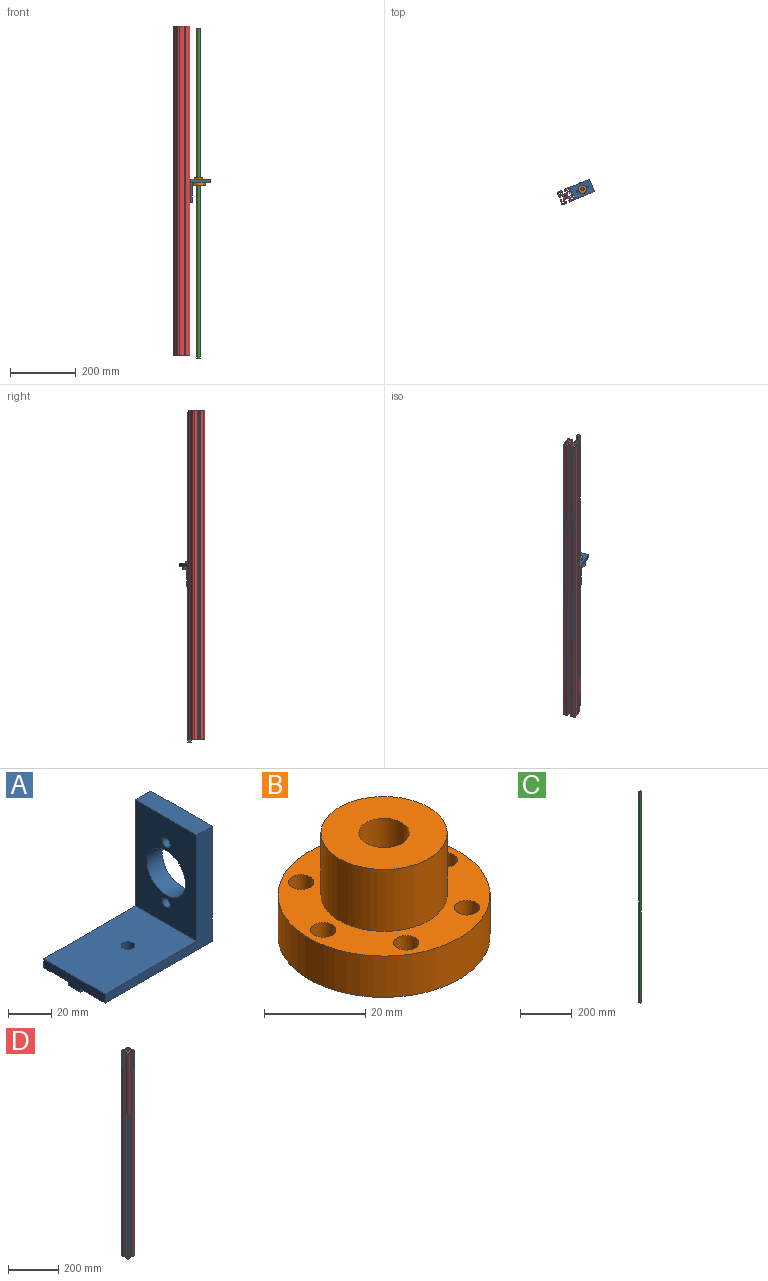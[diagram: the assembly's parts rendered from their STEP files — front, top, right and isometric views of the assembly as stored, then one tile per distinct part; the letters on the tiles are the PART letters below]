
ASSEMBLY  parts=4 mates=3
PART A: 16 faces, bbox 70x40x67 mm
  f0: plane 70x16.05mm, normal (0,0,-1), area 1123.5mm2, adj f1,f2,f3,f7
  f1: plane 40x7mm, normal (-1,0,0), area 215.8mm2, adj f0,f2,f4,f5,f6,f7,f8,f9
  f2: plane 70x65mm, normal (0,-1,0), area 950mm2, adj f0,f1,f3,f5,f11,f12
  f3: plane 67x40mm, normal (1,0,0), area 2079.7mm2, adj f0,f2,f4,f6,f7,f8,f9,f12
  f4: plane 70x65mm, normal (0,1,0), area 950mm2, adj f1,f3,f5,f6,f11,f12
  f5: plane 60x40mm, normal (0,0,1), area 2369.8mm2, adj f1,f2,f4,f10,f11
  f6: plane 70x16.05mm, normal (0,0,-1), area 1123.5mm2, adj f1,f3,f4,f8
  f7: plane 70x2mm, normal (0,-1,0), area 140mm2, adj f0,f1,f3,f9
  f8: plane 70x2mm, normal (0,1,0), area 140mm2, adj f1,f3,f6,f9
  f9: plane 70x7.9mm, normal (0,0,-1), area 522.8mm2, adj f1,f3,f7,f8,f10
  f10: cylinder r=3.1mm len=7mm, axis (0,0,-1), area 136.3mm2, adj f5,f9
  f11: plane 60x40mm, normal (-1,0,0), area 1863.9mm2, adj f2,f4,f5,f12,f13,f14,f15
  f12: plane 40x10mm, normal (0,0,1), area 400mm2, adj f2,f3,f4,f11
  f13: cylinder r=12.57mm len=25.15mm, axis (1,0,0), area 790.1mm2, adj f3,f11
  f14: cylinder r=2.5mm len=10mm, axis (-1,0,0), area 157.1mm2, adj f3,f11
  f15: cylinder r=2.5mm len=10mm, axis (-1,0,0), area 157.1mm2, adj f3,f11
PART B: 12 faces, bbox 42x42x25 mm
  f0: cylinder r=21mm len=42mm, axis (0,0,1), area 1319.5mm2, adj f1,f2
  f1: plane 42x42mm, normal (0,0,-1), area 1189.1mm2, adj f0,f5,f6,f7,f8,f9,f10,f11
  f2: plane 42x42mm, normal (0,0,1), area 776.8mm2, adj f0,f3,f6,f7,f8,f9,f10,f11
  f3: cylinder r=12.5mm len=25mm, axis (0,0,-1), area 1178.1mm2, adj f2,f4
  f4: plane 25x25mm, normal (0,0,1), area 412.3mm2, adj f3,f5
  f5: cylinder r=5mm len=25mm, axis (0,0,1), area 785.4mm2, adj f1,f4
  f6: cylinder r=2.5mm len=10mm, axis (0,0,-1), area 157.1mm2, adj f1,f2
  f7: cylinder r=2.5mm len=10mm, axis (0,0,-1), area 157.1mm2, adj f1,f2
  f8: cylinder r=2.5mm len=10mm, axis (0,0,-1), area 157.1mm2, adj f1,f2
  f9: cylinder r=2.5mm len=10mm, axis (0,0,-1), area 157.1mm2, adj f1,f2
  f10: cylinder r=2.5mm len=10mm, axis (0,0,-1), area 157.1mm2, adj f1,f2
  f11: cylinder r=2.5mm len=10mm, axis (0,0,-1), area 157.1mm2, adj f1,f2
PART C: 3 faces, bbox 10x10x1000 mm
  f0: cylinder r=5mm len=1000mm, axis (0,0,-1), area 31415.9mm2, adj f1,f2
  f1: plane 10x10mm, normal (0,0,1), area 78.5mm2, adj f0
  f2: plane 10x10mm, normal (0,0,-1), area 78.5mm2, adj f0
PART D: 87 faces, bbox 40x40x1000 mm
  f0: plane 1000x4mm, normal (0,-1,0), area 4000mm2, adj f1,f79,f85,f86
  f1: plane 1000x6mm, normal (-1,0,0), area 6000mm2, adj f0,f2,f85,f86
  f2: plane 1000x6mm, normal (0,1,0), area 6000mm2, adj f1,f3,f85,f86
  f3: plane 1000x4mm, normal (1,0,0), area 4000mm2, adj f2,f79,f85,f86
  f4: plane 1000x4mm, normal (0,1,0), area 4000mm2, adj f5,f80,f85,f86
  f5: plane 1000x6mm, normal (1,0,0), area 6000mm2, adj f4,f6,f85,f86
  f6: plane 1000x6mm, normal (0,-1,0), area 6000mm2, adj f5,f7,f85,f86
  f7: plane 1000x4mm, normal (-1,0,0), area 4000mm2, adj f6,f80,f85,f86
  f8: plane 1000x4mm, normal (1,0,0), area 4000mm2, adj f9,f81,f85,f86
  f9: plane 1000x6mm, normal (0,-1,0), area 6000mm2, adj f8,f10,f85,f86
  f10: plane 1000x6mm, normal (-1,0,0), area 6000mm2, adj f9,f11,f85,f86
  f11: plane 1000x4mm, normal (0,1,0), area 4000mm2, adj f10,f81,f85,f86
  f12: plane 1000x4mm, normal (-1,0,0), area 4000mm2, adj f13,f82,f85,f86
  f13: plane 1000x6mm, normal (0,1,0), area 6000mm2, adj f12,f14,f85,f86
  f14: plane 1000x6mm, normal (1,0,0), area 6000mm2, adj f13,f15,f85,f86
  f15: plane 1000x4mm, normal (0,-1,0), area 4000mm2, adj f14,f82,f85,f86
  f16: plane 1000x4.5mm, normal (0,-1,0), area 4500mm2, adj f17,f83,f85,f86
  f17: plane 1000x12mm, normal (1,0,0), area 12000mm2, adj f16,f18,f85,f86
  f18: cylinder r=4mm len=1000mm, axis (0,0,-1), area 6283.2mm2, adj f17,f19,f85,f86
  f19: plane 1000x12mm, normal (0,1,0), area 12000mm2, adj f18,f20,f85,f86
  f20: plane 1000x4.5mm, normal (-1,0,0), area 4500mm2, adj f19,f21,f85,f86
  f21: plane 1000x2.72mm, normal (0,-1,0), area 2717.9mm2, adj f20,f22,f85,f86
  f22: plane 1000x1.85mm, normal (1,0,0), area 1850mm2, adj f21,f23,f85,f86
  f23: plane 1000x3.5mm, normal (0,-1,0), area 3503mm2, adj f22,f24,f85,f86
  f24: plane 1000x5.35mm, normal (-1,0,0), area 5350mm2, adj f23,f25,f85,f86
  f25: plane 1000x6.22mm, normal (-0.56,0.83,0), area 7534.1mm2, adj f24,f26,f85,f86
  f26: plane 1000x8mm, normal (0,1,0), area 8000mm2, adj f25,f27,f85,f86
  f27: plane 1000x6.22mm, normal (0.56,0.83,0), area 7534.1mm2, adj f26,f28,f85,f86
  f28: plane 1000x5.35mm, normal (1,0,0), area 5350mm2, adj f27,f29,f85,f86
  f29: plane 1000x3.5mm, normal (0,-1,0), area 3503mm2, adj f28,f30,f85,f86
  f30: plane 1000x1.85mm, normal (-1,0,0), area 1850mm2, adj f29,f31,f85,f86
  f31: plane 1000x2.72mm, normal (0,-1,0), area 2717.9mm2, adj f30,f32,f85,f86
  f32: plane 1000x4.5mm, normal (1,0,0), area 4500mm2, adj f31,f33,f85,f86
  f33: plane 1000x12mm, normal (0,1,0), area 12000mm2, adj f32,f34,f85,f86
  f34: cylinder r=4mm len=1000mm, axis (0,0,-1), area 6283.2mm2, adj f33,f35,f85,f86
  f35: plane 1000x12mm, normal (-1,0,0), area 12000mm2, adj f34,f36,f85,f86
  f36: plane 1000x4.5mm, normal (0,-1,0), area 4500mm2, adj f35,f37,f85,f86
  f37: plane 1000x2.72mm, normal (1,0,0), area 2717.9mm2, adj f36,f38,f85,f86
  f38: plane 1000x1.85mm, normal (0,1,0), area 1850mm2, adj f37,f39,f85,f86
  f39: plane 1000x3.5mm, normal (1,0,0), area 3503mm2, adj f38,f40,f85,f86
  f40: plane 1000x5.35mm, normal (0,-1,0), area 5350mm2, adj f39,f41,f85,f86
  f41: plane 1000x6.22mm, normal (-0.83,-0.56,0), area 7534.1mm2, adj f40,f42,f85,f86
  f42: plane 1000x8mm, normal (-1,0,0), area 8000mm2, adj f41,f43,f85,f86
  f43: plane 1000x6.22mm, normal (-0.83,0.56,0), area 7534.1mm2, adj f42,f44,f85,f86
  f44: plane 1000x5.35mm, normal (0,1,0), area 5350mm2, adj f43,f45,f85,f86
  f45: plane 1000x3.5mm, normal (1,0,0), area 3503mm2, adj f44,f46,f85,f86
  f46: plane 1000x1.85mm, normal (0,-1,0), area 1850mm2, adj f45,f47,f85,f86
  f47: plane 1000x2.72mm, normal (1,0,0), area 2717.9mm2, adj f46,f48,f85,f86
  f48: plane 1000x4.5mm, normal (0,1,0), area 4500mm2, adj f47,f49,f85,f86
  f49: plane 1000x12mm, normal (-1,0,0), area 12000mm2, adj f48,f50,f85,f86
  f50: cylinder r=4mm len=1000mm, axis (0,0,-1), area 6283.2mm2, adj f49,f51,f85,f86
  f51: plane 1000x12mm, normal (0,-1,0), area 12000mm2, adj f50,f52,f85,f86
  f52: plane 1000x4.5mm, normal (1,0,0), area 4500mm2, adj f51,f53,f85,f86
  f53: plane 1000x2.72mm, normal (0,1,0), area 2717.9mm2, adj f52,f54,f85,f86
  f54: plane 1000x1.85mm, normal (-1,0,0), area 1850mm2, adj f53,f55,f85,f86
  f55: plane 1000x3.5mm, normal (0,1,0), area 3503mm2, adj f54,f56,f85,f86
  f56: plane 1000x5.35mm, normal (1,0,0), area 5350mm2, adj f55,f57,f85,f86
  f57: plane 1000x6.22mm, normal (0.56,-0.83,0), area 7534.1mm2, adj f56,f58,f85,f86
  f58: plane 1000x8mm, normal (0,-1,0), area 8000mm2, adj f57,f59,f85,f86
  f59: plane 1000x6.22mm, normal (-0.56,-0.83,0), area 7534.1mm2, adj f58,f60,f85,f86
  f60: plane 1000x5.35mm, normal (-1,0,0), area 5350mm2, adj f59,f61,f85,f86
  f61: plane 1000x3.5mm, normal (0,1,0), area 3503mm2, adj f60,f62,f85,f86
  f62: plane 1000x1.85mm, normal (1,0,0), area 1850mm2, adj f61,f63,f85,f86
  f63: plane 1000x2.72mm, normal (0,1,0), area 2717.9mm2, adj f62,f64,f85,f86
  f64: plane 1000x4.5mm, normal (-1,0,0), area 4500mm2, adj f63,f65,f85,f86
  f65: plane 1000x12mm, normal (0,-1,0), area 12000mm2, adj f64,f66,f85,f86
  f66: cylinder r=4mm len=1000mm, axis (0,0,-1), area 6283.2mm2, adj f65,f67,f85,f86
  f67: plane 1000x12mm, normal (1,0,0), area 12000mm2, adj f66,f68,f85,f86
  f68: plane 1000x4.5mm, normal (0,1,0), area 4500mm2, adj f67,f69,f85,f86
  f69: plane 1000x2.72mm, normal (-1,0,0), area 2717.9mm2, adj f68,f70,f85,f86
  f70: plane 1000x1.85mm, normal (0,-1,0), area 1850mm2, adj f69,f71,f85,f86
  f71: plane 1000x3.5mm, normal (-1,0,0), area 3503mm2, adj f70,f72,f85,f86
  f72: plane 1000x5.35mm, normal (0,1,0), area 5350mm2, adj f71,f73,f85,f86
  f73: plane 1000x6.22mm, normal (0.83,0.56,0), area 7534.1mm2, adj f72,f74,f85,f86
  f74: plane 1000x8mm, normal (1,0,0), area 8000mm2, adj f73,f75,f85,f86
  f75: plane 1000x6.22mm, normal (0.83,-0.56,0), area 7534.1mm2, adj f74,f76,f85,f86
  f76: plane 1000x5.35mm, normal (0,-1,0), area 5350mm2, adj f75,f77,f85,f86
  f77: plane 1000x3.5mm, normal (-1,0,0), area 3503mm2, adj f76,f78,f85,f86
  f78: plane 1000x1.85mm, normal (0,1,0), area 1850mm2, adj f77,f83,f85,f86
  f79: cylinder r=2mm len=1000mm, axis (0,0,-1), area 3141.6mm2, adj f0,f3,f85,f86
  f80: cylinder r=2mm len=1000mm, axis (0,0,-1), area 3141.6mm2, adj f4,f7,f85,f86
  f81: cylinder r=2mm len=1000mm, axis (0,0,-1), area 3141.6mm2, adj f8,f11,f85,f86
  f82: cylinder r=2mm len=1000mm, axis (0,0,-1), area 3141.6mm2, adj f12,f15,f85,f86
  f83: plane 1000x2.72mm, normal (-1,0,0), area 2717.9mm2, adj f16,f78,f85,f86
  f84: cylinder r=3.4mm len=1000mm, axis (0,0,-1), area 21362.8mm2, adj f85,f86
  f85: plane 40x40mm, normal (0,0,1), area 685.6mm2, adj f0,f1,f2,f3,f4,f5,f6,f7
  f86: plane 40x40mm, normal (0,0,-1), area 685.6mm2, adj f0,f1,f2,f3,f4,f5,f6,f7
PLACE A rot(axis=(-0.7,-0.14,-0.7),164.1deg) t=(-316.24,153.66,517.99)mm
PLACE B rot(axis=(0,0,1),22.5deg) t=(-277.51,148.07,577.99)mm
PLACE C rot(axis=(0,0,1),125.2deg) t=(-277.51,148.07,45.13)mm
PLACE D rot(axis=(0.2,-0.98,0),180deg) t=(-328.9,126.76,1052.99)mm
MATE fastened B.f0 <-> A.f13  axis (0,0,1) through (-277.51,148.07,577.99)mm
MATE cylindrical B.f0 <-> C.f0  axis (0,0,-1) through (-277.51,148.07,567.99)mm
MATE fastened A.f10 <-> D.f35  axis (-0.92,-0.38,0) through (-310.43,134.42,552.99)mm
